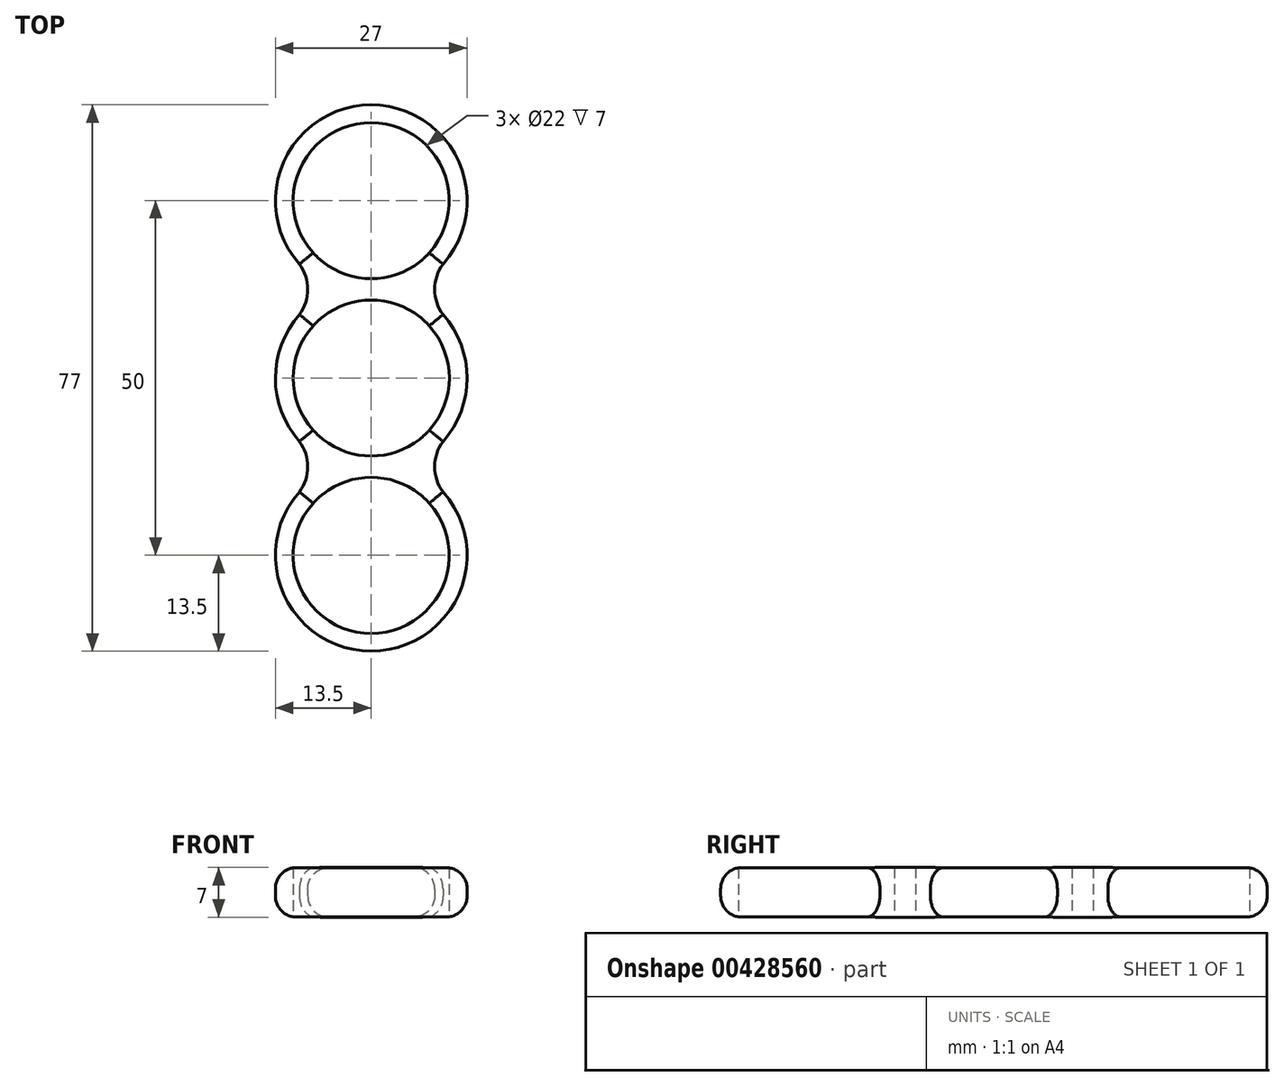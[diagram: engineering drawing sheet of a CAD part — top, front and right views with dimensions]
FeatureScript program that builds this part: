
annotation { "Feature Type Name" : "Feature", "Feature Type Description" : "" }
export const myFeature = defineFeature(function(context is Context, id is Id, definition is map)
    precondition{}
    {
        {
            var Q0;
            Q0=qCreatedBy(makeId("Top.planeOp"),FACE);
            var sketch = newSketch(context, id + "F0", { "sketchPlane" : qUnion([Q0])});
            skCircle(sketch, "E0", {"center": v(0, 0) * mm, "radius": 13.5 * mm});
            skCircle(sketch, "E1", {"center": v(0, 25) * mm, "radius": 13.5 * mm});
            skCircle(sketch, "E2", {"center": v(0, -25) * mm, "radius": 13.5 * mm});
            skCircle(sketch, "E3", {"center": v(0, 25) * mm, "radius": 11 * mm});
            skCircle(sketch, "E4", {"center": v(0, 0) * mm, "radius": 11 * mm});
            skCircle(sketch, "E5", {"center": v(0, -25) * mm, "radius": 11 * mm});
            skLineSegment(sketch, "E6", {"start": v(0, 25) * mm, "end": v(0, 0) * mm});
            skLineSegment(sketch, "E7", {"start": v(0, 0) * mm, "end": v(0, -25) * mm});
            skLineSegment(sketch, "E8.bottom", {"start": v(10.11, 16.06) * mm, "end": v(-10.11, 16.06) * mm});
            skLineSegment(sketch, "E8.top", {"start": v(10.11, -16.06) * mm, "end": v(-10.11, -16.06) * mm});
            skLineSegment(sketch, "E8.left", {"start": v(10.11, 16.06) * mm, "end": v(10.11, -16.06) * mm});
            skLineSegment(sketch, "E8.right", {"start": v(-10.11, 16.06) * mm, "end": v(-10.11, -16.06) * mm});
            skArc(sketch, "E9", {"start": v(-10.11, 8.94) * mm, "mid": v(-8.94, 12.5) * mm, "end": v(-10.11, 16.06) * mm});
            skArc(sketch, "E10", {"start": v(10.11, 16.06) * mm, "mid": v(8.94, 12.5) * mm, "end": v(10.11, 8.94) * mm});
            skArc(sketch, "E11", {"start": v(10.11, -8.94) * mm, "mid": v(8.94, -12.5) * mm, "end": v(10.11, -16.06) * mm});
            skArc(sketch, "E12", {"start": v(-10.11, -16.06) * mm, "mid": v(-8.94, -12.5) * mm, "end": v(-10.11, -8.94) * mm});
            skSolve(sketch);
        }
        {
            var Q0;
            Q0=makeQuery(id+"F0.imprint","IMPRINT",FACE,{"disambiguationData":[TD([[makeQuery(id+"F0.imprint","IMPRINT",EDGE,{"derivedFrom":sQuery(id+"F0.wireOp",EDGE,"E3")}),-1.0]])]});
            var Q1;
            Q1=makeQuery(id+"F0.imprint","IMPRINT",FACE,{"disambiguationData":[TD([[makeQuery(id+"F0.imprint","IMPRINT",EDGE,{"derivedFrom":sQuery(id+"F0.wireOp",EDGE,"E4")}),-1.0]])]});
            var Q2;
            {var subQ0=sQuery(id+"F0.wireOp",EDGE,"8NVjbOzX-PMFP-SMiF-mR44-4HxgfJyXqWLy");Q2=makeQuery(id+"F0.imprint","IMPRINT",FACE,{"disambiguationData":[TD([[makeQuery(id+"F0.imprint","IMPRINT",EDGE,{"derivedFrom":subQ0}),-1.0]])]});}
            var Q3;
            {var subQ0=sQuery(id+"F0.wireOp",EDGE,"8D0jgICW-DnKe-v4Jl-ZKUK-Z3WR8P1peYuu");Q3=makeQuery(id+"F0.imprint","IMPRINT",FACE,{"disambiguationData":[TD([[makeQuery(id+"F0.imprint","IMPRINT",EDGE,{"derivedFrom":subQ0}),-1.0]])]});}
            var Q4;
            {var subQ0=sQuery(id+"F0.wireOp",EDGE,"lii5ZDwy-MTPm-D6Ey-s2wq-PMPPb5O6u5Qs");Q4=makeQuery(id+"F0.imprint","IMPRINT",FACE,{"disambiguationData":[TD([[makeQuery(id+"F0.imprint","IMPRINT",EDGE,{"derivedFrom":subQ0}),-1.0]])]});}
            var Q5;
            Q5=makeQuery(id+"F0.imprint","IMPRINT",FACE,{"disambiguationData":[TD([[makeQuery(id+"F0.imprint","IMPRINT",EDGE,{"derivedFrom":sQuery(id+"F0.wireOp",EDGE,"E5")}),-1.0]])]});
            var Q6;
            {var subQ0=sQuery(id+"F0.wireOp",EDGE,"DoshLFPW-BsUl-09P3-fBDv-4gjIutWCNOgP");Q6=makeQuery(id+"F0.imprint","IMPRINT",FACE,{"disambiguationData":[TD([[makeQuery(id+"F0.imprint","IMPRINT",EDGE,{"derivedFrom":subQ0}),-1.0]])]});}
            var Q7;
            {var subQ0=sQuery(id+"F0.wireOp",EDGE,"Gda6w7I7-AgMa-eA2T-BYnE-LKXL9i1t3kz7");var subQ1=sQuery(id+"F0.wireOp",EDGE,"E0");var subQ2=makeQuery(id+"F0.imprint","INTERSECT",VERTEX,{"disambiguationData":[OD(1.0)],"derivedFrom":[subQ1,subQ0]});Q7=makeQuery(id+"F0.imprint","IMPRINT",FACE,{"disambiguationData":[TD([[makeQuery(id+"F0.imprint","IMPRINT",EDGE,{"disambiguationData":[TD([[subQ2,-1.0]])],"derivedFrom":subQ0}),-1.0]])]});}
            var Q8;
            {var subQ0=sQuery(id+"F0.wireOp",EDGE,"VBNOPyqx-pYbB-zUJ9-EXDc-pKWEcQx94P10");var subQ1=sQuery(id+"F0.wireOp",EDGE,"E0");var subQ2=makeQuery(id+"F0.imprint","INTERSECT",VERTEX,{"disambiguationData":[OD(1.0)],"derivedFrom":[subQ1,subQ0]});Q8=makeQuery(id+"F0.imprint","IMPRINT",FACE,{"disambiguationData":[TD([[makeQuery(id+"F0.imprint","IMPRINT",EDGE,{"disambiguationData":[TD([[subQ2,1.0]])],"derivedFrom":subQ0}),-1.0]])]});}
            var Q9;
            {var subQ0=sQuery(id+"F0.wireOp",EDGE,"nJaVq4tj-WkV2-JixM-sRQs-WNpxJVOSEhEY");var subQ1=sQuery(id+"F0.wireOp",EDGE,"E0");var subQ2=makeQuery(id+"F0.imprint","INTERSECT",VERTEX,{"disambiguationData":[OD(1.0)],"derivedFrom":[subQ1,subQ0]});Q9=makeQuery(id+"F0.imprint","IMPRINT",FACE,{"disambiguationData":[TD([[makeQuery(id+"F0.imprint","IMPRINT",EDGE,{"disambiguationData":[TD([[subQ2,-1.0]])],"derivedFrom":subQ0}),-1.0]])]});}
            var Q10;
            {var subQ0=sQuery(id+"F0.wireOp",EDGE,"bMmc7eOJ-D6uA-E2Za-5PyS-XfN60Q22Ys6g");var subQ1=sQuery(id+"F0.wireOp",EDGE,"E0");var subQ2=makeQuery(id+"F0.imprint","INTERSECT",VERTEX,{"disambiguationData":[OD(1.0)],"derivedFrom":[subQ1,subQ0]});Q10=makeQuery(id+"F0.imprint","IMPRINT",FACE,{"disambiguationData":[TD([[makeQuery(id+"F0.imprint","IMPRINT",EDGE,{"disambiguationData":[TD([[subQ2,1.0]])],"derivedFrom":subQ0}),-1.0]])]});}
            var Q11;
            {var subQ0=sQuery(id+"F0.wireOp",EDGE,"E6");var subQ1=sQuery(id+"F0.wireOp",EDGE,"E0");var subQ2=makeQuery(id+"F0.imprint","INTERSECT",VERTEX,{"derivedFrom":[subQ1,subQ0]});Q11=makeQuery(id+"F0.imprint","IMPRINT",FACE,{"disambiguationData":[TD([[makeQuery(id+"F0.imprint","IMPRINT",EDGE,{"disambiguationData":[TD([[subQ2,1.0]])],"derivedFrom":subQ1}),1.0]])]});}
            var Q12;
            {var subQ0=sQuery(id+"F0.wireOp",EDGE,"E6");var subQ1=sQuery(id+"F0.wireOp",EDGE,"E0");var subQ2=makeQuery(id+"F0.imprint","INTERSECT",VERTEX,{"derivedFrom":[subQ1,subQ0]});Q12=makeQuery(id+"F0.imprint","IMPRINT",FACE,{"disambiguationData":[TD([[makeQuery(id+"F0.imprint","IMPRINT",EDGE,{"disambiguationData":[TD([[subQ2,-1.0]])],"derivedFrom":subQ1}),1.0]])]});}
            var Q13;
            {var subQ0=sQuery(id+"F0.wireOp",EDGE,"E2");var subQ1=sQuery(id+"F0.wireOp",EDGE,"E0");var subQ2=makeQuery(id+"F0.imprint","INTERSECT",VERTEX,{"disambiguationData":[OD(0.0)],"derivedFrom":[subQ1,subQ0]});Q13=makeQuery(id+"F0.imprint","IMPRINT",FACE,{"disambiguationData":[TD([[makeQuery(id+"F0.imprint","IMPRINT",EDGE,{"disambiguationData":[TD([[subQ2,-1.0]])],"derivedFrom":subQ1}),1.0]])]});}
            var Q14;
            {var subQ0=sQuery(id+"F0.wireOp",EDGE,"E7");var subQ1=sQuery(id+"F0.wireOp",EDGE,"E0");var subQ2=makeQuery(id+"F0.imprint","INTERSECT",VERTEX,{"derivedFrom":[subQ1,subQ0]});Q14=makeQuery(id+"F0.imprint","IMPRINT",FACE,{"disambiguationData":[TD([[makeQuery(id+"F0.imprint","IMPRINT",EDGE,{"disambiguationData":[TD([[subQ2,-1.0]])],"derivedFrom":subQ1}),1.0]])]});}
            var Q15;
            {var subQ0=sQuery(id+"F0.wireOp",EDGE,"E6");var subQ1=sQuery(id+"F0.wireOp",EDGE,"E0");var subQ2=makeQuery(id+"F0.imprint","INTERSECT",VERTEX,{"derivedFrom":[subQ1,subQ0]});Q15=makeQuery(id+"F0.imprint","IMPRINT",FACE,{"disambiguationData":[TD([[makeQuery(id+"F0.imprint","IMPRINT",EDGE,{"disambiguationData":[TD([[subQ2,-1.0]])],"derivedFrom":subQ1}),-1.0]])]});}
            var Q16;
            {var subQ1=sQuery(id+"F0.wireOp",EDGE,"E0");var subQ6=sQuery(id+"F0.wireOp",EDGE,"E1");var subQ8=makeQuery(id+"F0.imprint","INTERSECT",VERTEX,{"disambiguationData":[OD(0.0)],"derivedFrom":[subQ1,subQ6]});Q16=makeQuery(id+"F0.imprint","IMPRINT",FACE,{"disambiguationData":[TD([[makeQuery(id+"F0.imprint","IMPRINT",EDGE,{"disambiguationData":[TD([[subQ8,-1.0]])],"derivedFrom":subQ1}),-1.0]])]});}
            var Q17;
            {var subQ0=sQuery(id+"F0.wireOp",EDGE,"E10");Q17=makeQuery(id+"F0.imprint","IMPRINT",FACE,{"disambiguationData":[TD([[makeQuery(id+"F0.imprint","IMPRINT",EDGE,{"derivedFrom":subQ0}),-1.0]])]});}
            var Q18;
            {var subQ5=sQuery(id+"F0.wireOp",EDGE,"E1");var subQ6=sQuery(id+"F0.wireOp",EDGE,"E0");var subQ7=makeQuery(id+"F0.imprint","INTERSECT",VERTEX,{"disambiguationData":[OD(0.0)],"derivedFrom":[subQ6,subQ5]});Q18=makeQuery(id+"F0.imprint","IMPRINT",FACE,{"disambiguationData":[TD([[makeQuery(id+"F0.imprint","IMPRINT",EDGE,{"disambiguationData":[TD([[subQ7,1.0]])],"derivedFrom":subQ5}),-1.0]])]});}
            var Q19;
            {var subQ1=sQuery(id+"F0.wireOp",EDGE,"E1");var subQ7=sQuery(id+"F0.wireOp",EDGE,"E0");var subQ8=makeQuery(id+"F0.imprint","INTERSECT",VERTEX,{"disambiguationData":[OD(1.0)],"derivedFrom":[subQ7,subQ1]});Q19=makeQuery(id+"F0.imprint","IMPRINT",FACE,{"disambiguationData":[TD([[makeQuery(id+"F0.imprint","IMPRINT",EDGE,{"disambiguationData":[TD([[subQ8,-1.0]])],"derivedFrom":subQ1}),-1.0]])]});}
            var Q20;
            {var subQ0=sQuery(id+"F0.wireOp",EDGE,"E9");Q20=makeQuery(id+"F0.imprint","IMPRINT",FACE,{"disambiguationData":[TD([[makeQuery(id+"F0.imprint","IMPRINT",EDGE,{"derivedFrom":subQ0}),-1.0]])]});}
            var Q21;
            {var subQ0=sQuery(id+"F0.wireOp",EDGE,"E12");Q21=makeQuery(id+"F0.imprint","IMPRINT",FACE,{"disambiguationData":[TD([[makeQuery(id+"F0.imprint","IMPRINT",EDGE,{"derivedFrom":subQ0}),-1.0]])]});}
            var Q22;
            {var subQ1=sQuery(id+"F0.wireOp",EDGE,"E2");var subQ6=sQuery(id+"F0.wireOp",EDGE,"E0");var subQ8=makeQuery(id+"F0.imprint","INTERSECT",VERTEX,{"disambiguationData":[OD(0.0)],"derivedFrom":[subQ6,subQ1]});Q22=makeQuery(id+"F0.imprint","IMPRINT",FACE,{"disambiguationData":[TD([[makeQuery(id+"F0.imprint","IMPRINT",EDGE,{"disambiguationData":[TD([[subQ8,1.0]])],"derivedFrom":subQ1}),-1.0]])]});}
            var Q23;
            {var subQ5=sQuery(id+"F0.wireOp",EDGE,"E2");var subQ6=sQuery(id+"F0.wireOp",EDGE,"E0");var subQ7=makeQuery(id+"F0.imprint","INTERSECT",VERTEX,{"disambiguationData":[OD(1.0)],"derivedFrom":[subQ6,subQ5]});Q23=makeQuery(id+"F0.imprint","IMPRINT",FACE,{"disambiguationData":[TD([[makeQuery(id+"F0.imprint","IMPRINT",EDGE,{"disambiguationData":[TD([[subQ7,-1.0]])],"derivedFrom":subQ5}),-1.0]])]});}
            var Q24;
            {var subQ0=sQuery(id+"F0.wireOp",EDGE,"E11");Q24=makeQuery(id+"F0.imprint","IMPRINT",FACE,{"disambiguationData":[TD([[makeQuery(id+"F0.imprint","IMPRINT",EDGE,{"derivedFrom":subQ0}),-1.0]])]});}
            var Q25;
            {var subQ0=sQuery(id+"F0.wireOp",EDGE,"E7");var subQ5=sQuery(id+"F0.wireOp",EDGE,"E0");var subQ6=makeQuery(id+"F0.imprint","INTERSECT",VERTEX,{"derivedFrom":[subQ5,subQ0]});Q25=makeQuery(id+"F0.imprint","IMPRINT",FACE,{"disambiguationData":[TD([[makeQuery(id+"F0.imprint","IMPRINT",EDGE,{"disambiguationData":[TD([[subQ6,-1.0]])],"derivedFrom":subQ5}),-1.0]])]});}
            var Q26;
            {var subQ1=sQuery(id+"F0.wireOp",EDGE,"E0");var subQ6=sQuery(id+"F0.wireOp",EDGE,"E2");var subQ8=makeQuery(id+"F0.imprint","INTERSECT",VERTEX,{"disambiguationData":[OD(0.0)],"derivedFrom":[subQ1,subQ6]});Q26=makeQuery(id+"F0.imprint","IMPRINT",FACE,{"disambiguationData":[TD([[makeQuery(id+"F0.imprint","IMPRINT",EDGE,{"disambiguationData":[TD([[subQ8,-1.0]])],"derivedFrom":subQ1}),-1.0]])]});}
            extrude(context, id + "F1", {"entities" : qUnion([Q0, Q1, Q2, Q3, Q4, Q5, Q6, Q7, Q8, Q9, Q10, Q11, Q12, Q13, Q14, Q15, Q16, Q17, Q18, Q19, Q20, Q21, Q22, Q23, Q24, Q25, Q26]), "depth" : 7 * mm});
        }
        {
            var Q0;
            Q0=makeQuery(id+"F1.opExtrude","CAP_EDGE",EDGE,{"disambiguationData":[OSD([sQuery(id+"F0.wireOp",EDGE,"E1")])],"isStart":false});
            var Q1;
            Q1=makeQuery(id+"F1.opExtrude","CAP_EDGE",EDGE,{"disambiguationData":[OSD([sQuery(id+"F0.wireOp",EDGE,"E9")])],"isStart":false});
            var Q2;
            {var subQ0=sQuery(id+"F0.wireOp",EDGE,"E8.right");var subQ1=sQuery(id+"F0.wireOp",EDGE,"E0");Q2=makeQuery(id+"F1.opExtrude","CAP_EDGE",EDGE,{"disambiguationData":[OSD([subQ1]),TDD([makeQuery(id+"F0.imprint","IMPRINT",EDGE,{"disambiguationData":[TD([[makeQuery(id+"F0.imprint","INTERSECT",VERTEX,{"derivedFrom":[subQ1,subQ0,sQuery(id+"F0.wireOp",EDGE,"E9")]}),-1.0]])],"derivedFrom":subQ1})])],"isStart":false});}
            var Q3;
            Q3=makeQuery(id+"F1.opExtrude","CAP_EDGE",EDGE,{"disambiguationData":[OSD([sQuery(id+"F0.wireOp",EDGE,"E10")])],"isStart":false});
            var Q4;
            {var subQ0=sQuery(id+"F0.wireOp",EDGE,"E8.left");var subQ1=sQuery(id+"F0.wireOp",EDGE,"E0");Q4=makeQuery(id+"F1.opExtrude","CAP_EDGE",EDGE,{"disambiguationData":[OSD([subQ1]),TDD([makeQuery(id+"F0.imprint","IMPRINT",EDGE,{"disambiguationData":[TD([[makeQuery(id+"F0.imprint","INTERSECT",VERTEX,{"derivedFrom":[subQ1,subQ0,sQuery(id+"F0.wireOp",EDGE,"E10")]}),1.0]])],"derivedFrom":subQ1})])],"isStart":false});}
            var Q5;
            Q5=makeQuery(id+"F1.opExtrude","CAP_EDGE",EDGE,{"disambiguationData":[OSD([sQuery(id+"F0.wireOp",EDGE,"E11")])],"isStart":false});
            var Q6;
            Q6=makeQuery(id+"F1.opExtrude","CAP_EDGE",EDGE,{"disambiguationData":[OSD([sQuery(id+"F0.wireOp",EDGE,"E2")])],"isStart":false});
            var Q7;
            Q7=makeQuery(id+"F1.opExtrude","CAP_EDGE",EDGE,{"disambiguationData":[OSD([sQuery(id+"F0.wireOp",EDGE,"E12")])],"isStart":false});
            fillet(context, id + "F2", {"entities" : qUnion([Q0, Q1, Q2, Q3, Q4, Q5, Q6, Q7]), "radius" : 3 * mm, "tangentPropagation" : true, "allowEdgeOverflow" : false});
        }
        {
            var Q0;
            Q0=makeQuery(id+"F1.opExtrude","CAP_EDGE",EDGE,{"disambiguationData":[OSD([sQuery(id+"F0.wireOp",EDGE,"lii5ZDwy-MTPm-D6Ey-s2wq-PMPPb5O6u5Qs")])],"isStart":true});
            var Q1;
            Q1=makeQuery(id+"F1.opExtrude","CAP_EDGE",EDGE,{"disambiguationData":[OSD([sQuery(id+"F0.wireOp",EDGE,"DoshLFPW-BsUl-09P3-fBDv-4gjIutWCNOgP")])],"isStart":true});
            var Q2;
            {var subQ0=sQuery(id+"F0.wireOp",EDGE,"E0");Q2=makeQuery(id+"F1.opExtrude","CAP_EDGE",EDGE,{"disambiguationData":[OSD([subQ0]),TDD([makeQuery(id+"F0.imprint","IMPRINT",EDGE,{"disambiguationData":[TD([[makeQuery(id+"F0.imprint","INTERSECT",VERTEX,{"derivedFrom":[subQ0,sQuery(id+"F0.wireOp",EDGE,"8NVjbOzX-PMFP-SMiF-mR44-4HxgfJyXqWLy")]}),1.0]])],"derivedFrom":subQ0})])],"isStart":true});}
            var Q3;
            {var subQ0=sQuery(id+"F0.wireOp",EDGE,"E0");Q3=makeQuery(id+"F1.opExtrude","CAP_EDGE",EDGE,{"disambiguationData":[OSD([subQ0]),TDD([makeQuery(id+"F0.imprint","IMPRINT",EDGE,{"disambiguationData":[TD([[makeQuery(id+"F0.imprint","INTERSECT",VERTEX,{"derivedFrom":[subQ0,sQuery(id+"F0.wireOp",EDGE,"8D0jgICW-DnKe-v4Jl-ZKUK-Z3WR8P1peYuu")]}),-1.0]])],"derivedFrom":subQ0})])],"isStart":true});}
            var Q4;
            Q4=makeQuery(id+"F1.opExtrude","CAP_EDGE",EDGE,{"disambiguationData":[OSD([sQuery(id+"F0.wireOp",EDGE,"8D0jgICW-DnKe-v4Jl-ZKUK-Z3WR8P1peYuu")])],"isStart":true});
            var Q5;
            Q5=makeQuery(id+"F1.opExtrude","CAP_EDGE",EDGE,{"disambiguationData":[OSD([sQuery(id+"F0.wireOp",EDGE,"E1")])],"isStart":true});
            var Q6;
            Q6=makeQuery(id+"F1.opExtrude","CAP_EDGE",EDGE,{"disambiguationData":[OSD([sQuery(id+"F0.wireOp",EDGE,"8NVjbOzX-PMFP-SMiF-mR44-4HxgfJyXqWLy")])],"isStart":true});
            var Q7;
            Q7=makeQuery(id+"F1.opExtrude","CAP_EDGE",EDGE,{"disambiguationData":[OSD([sQuery(id+"F0.wireOp",EDGE,"Gda6w7I7-AgMa-eA2T-BYnE-LKXL9i1t3kz7")])],"isStart":true});
            var Q8;
            Q8=makeQuery(id+"F1.opExtrude","CAP_EDGE",EDGE,{"disambiguationData":[OSD([sQuery(id+"F0.wireOp",EDGE,"bMmc7eOJ-D6uA-E2Za-5PyS-XfN60Q22Ys6g")])],"isStart":true});
            var Q9;
            Q9=makeQuery(id+"F1.opExtrude","CAP_EDGE",EDGE,{"disambiguationData":[OSD([sQuery(id+"F0.wireOp",EDGE,"nJaVq4tj-WkV2-JixM-sRQs-WNpxJVOSEhEY")])],"isStart":true});
            var Q10;
            Q10=makeQuery(id+"F1.opExtrude","CAP_EDGE",EDGE,{"disambiguationData":[OSD([sQuery(id+"F0.wireOp",EDGE,"VBNOPyqx-pYbB-zUJ9-EXDc-pKWEcQx94P10")])],"isStart":true});
            var Q11;
            Q11=makeQuery(id+"F1.opExtrude","CAP_EDGE",EDGE,{"disambiguationData":[OSD([sQuery(id+"F0.wireOp",EDGE,"E9")])],"isStart":true});
            var Q12;
            {var subQ0=sQuery(id+"F0.wireOp",EDGE,"E8.right");var subQ1=sQuery(id+"F0.wireOp",EDGE,"E0");Q12=makeQuery(id+"F1.opExtrude","CAP_EDGE",EDGE,{"disambiguationData":[OSD([subQ1]),TDD([makeQuery(id+"F0.imprint","IMPRINT",EDGE,{"disambiguationData":[TD([[makeQuery(id+"F0.imprint","INTERSECT",VERTEX,{"derivedFrom":[subQ1,subQ0,sQuery(id+"F0.wireOp",EDGE,"E9")]}),-1.0]])],"derivedFrom":subQ1})])],"isStart":true});}
            var Q13;
            Q13=makeQuery(id+"F1.opExtrude","CAP_EDGE",EDGE,{"disambiguationData":[OSD([sQuery(id+"F0.wireOp",EDGE,"E12")])],"isStart":true});
            var Q14;
            Q14=makeQuery(id+"F1.opExtrude","CAP_EDGE",EDGE,{"disambiguationData":[OSD([sQuery(id+"F0.wireOp",EDGE,"E2")])],"isStart":true});
            var Q15;
            Q15=makeQuery(id+"F1.opExtrude","CAP_EDGE",EDGE,{"disambiguationData":[OSD([sQuery(id+"F0.wireOp",EDGE,"E11")])],"isStart":true});
            var Q16;
            {var subQ0=sQuery(id+"F0.wireOp",EDGE,"E8.left");var subQ1=sQuery(id+"F0.wireOp",EDGE,"E0");Q16=makeQuery(id+"F1.opExtrude","CAP_EDGE",EDGE,{"disambiguationData":[OSD([subQ1]),TDD([makeQuery(id+"F0.imprint","IMPRINT",EDGE,{"disambiguationData":[TD([[makeQuery(id+"F0.imprint","INTERSECT",VERTEX,{"derivedFrom":[subQ1,subQ0,sQuery(id+"F0.wireOp",EDGE,"E10")]}),1.0]])],"derivedFrom":subQ1})])],"isStart":true});}
            var Q17;
            Q17=makeQuery(id+"F1.opExtrude","CAP_EDGE",EDGE,{"disambiguationData":[OSD([sQuery(id+"F0.wireOp",EDGE,"E10")])],"isStart":true});
            fillet(context, id + "F3", {"entities" : qUnion([Q0, Q1, Q2, Q3, Q4, Q5, Q6, Q7, Q8, Q9, Q10, Q11, Q12, Q13, Q14, Q15, Q16, Q17]), "radius" : 3 * mm, "tangentPropagation" : true, "allowEdgeOverflow" : false});
        }
    });
